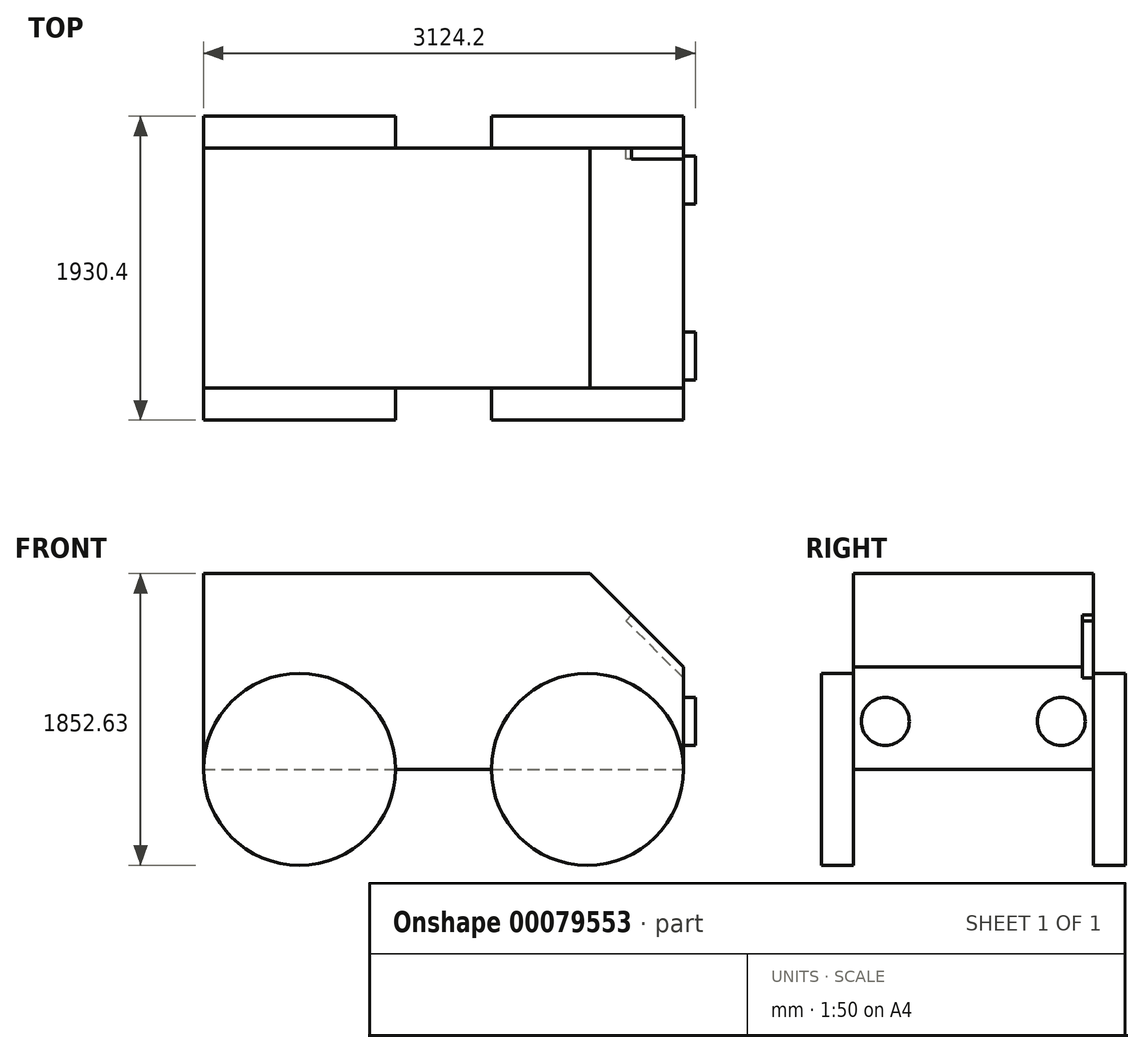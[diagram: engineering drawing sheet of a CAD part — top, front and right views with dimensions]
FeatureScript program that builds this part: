
annotation { "Feature Type Name" : "Feature", "Feature Type Description" : "" }
export const myFeature = defineFeature(function(context is Context, id is Id, definition is map)
    precondition{}
    {
        {
            var Q0;
            Q0=qCreatedBy(makeId("Front.planeOp"),FACE);
            var sketch = newSketch(context, id + "F0", { "sketchPlane" : qUnion([Q0])});
            skLineSegment(sketch, "E0", {"start": v(0, 0) * mm, "end": v(1522.8, 0) * mm});
            skLineSegment(sketch, "E1", {"start": v(1522.8, 0) * mm, "end": v(1522.8, 651.7) * mm});
            skLineSegment(sketch, "E2", {"start": v(1522.8, 651.7) * mm, "end": v(931.48, 1243.03) * mm});
            skLineSegment(sketch, "E3", {"start": v(931.48, 1243.03) * mm, "end": v(-1525.2, 1243.03) * mm});
            skLineSegment(sketch, "E4", {"start": v(-1525.2, 1243.03) * mm, "end": v(-1525.2, 0) * mm});
            skLineSegment(sketch, "E5", {"start": v(-1525.2, 0) * mm, "end": v(0, 0) * mm});
            skSolve(sketch);
        }
        {
            var Q0;
            Q0=makeQuery(id+"F0.imprint","IMPRINT",FACE,{"disambiguationData":[TD([[makeQuery(id+"F0.imprint","IMPRINT",EDGE,{"derivedFrom":sQuery(id+"F0.wireOp",EDGE,"E0")}),1.0]])]});
            extrude(context, id + "F1", {"entities" : qUnion([Q0]), "depth" : 1524 * mm});
        }
        {
            var Q0;
            Q0=makeQuery(id+"F1.opExtrude","SWEPT_FACE",FACE,{"disambiguationData":[OSD([sQuery(id+"F0.wireOp",EDGE,"E1")])]});
            var sketch = newSketch(context, id + "F2", { "sketchPlane" : qUnion([Q0])});
            skCircle(sketch, "E6", {"center": v(-203.2, 304.8) * mm, "radius": 152.4 * mm});
            skCircle(sketch, "E7", {"center": v(-1320.8, 304.8) * mm, "radius": 152.4 * mm});
            skSolve(sketch);
        }
        {
            var Q0;
            Q0 = qSketchRegion(id + "F2", true);
            extrude(context, id + "F3", {"entities" : qUnion([Q0]), "operationType" : NewBodyOperationType.ADD, "depth" : 76.2 * mm});
        }
        {
            var Q0;
            Q0=makeQuery(id+"F1.opExtrude","SWEPT_FACE",FACE,{"disambiguationData":[OSD([sQuery(id+"F0.wireOp",EDGE,"E2")])]});
            var sketch = newSketch(context, id + "F4", { "sketchPlane" : qUnion([Q0])});
            skLineSegment(sketch, "E8.bottom", {"start": v(-67.9, -1371.6) * mm, "end": v(463.56, -1371.6) * mm});
            skLineSegment(sketch, "E8.top", {"start": v(-67.9, -152.4) * mm, "end": v(463.56, -152.4) * mm});
            skLineSegment(sketch, "E8.left", {"start": v(-67.9, -1371.6) * mm, "end": v(-67.9, -152.4) * mm});
            skLineSegment(sketch, "E8.right", {"start": v(463.56, -1371.6) * mm, "end": v(463.56, -152.4) * mm});
            skSolve(sketch);
        }
        {
            var Q0;
            Q0 = qSketchRegion(id + "F4", true);
            extrude(context, id + "F5", {"entities" : qUnion([Q0]), "operationType" : NewBodyOperationType.REMOVE, "oppositeDirection" : true, "depth" : 50.8 * mm});
        }
        {
            var Q0;
            Q0=makeQuery(id+"F1.opExtrude","CAP_FACE",FACE,{"disambiguationData":[OSD([sQuery(id+"F0.wireOp",EDGE,"E0"),sQuery(id+"F0.wireOp",EDGE,"E1"),sQuery(id+"F0.wireOp",EDGE,"E2"),sQuery(id+"F0.wireOp",EDGE,"E3"),sQuery(id+"F0.wireOp",EDGE,"E4"),sQuery(id+"F0.wireOp",EDGE,"E5")])],"isStart":true});
            var sketch = newSketch(context, id + "F6", { "sketchPlane" : qUnion([Q0])});
            skCircle(sketch, "E9", {"center": v(-913.2, 0) * mm, "radius": 609.6 * mm});
            skCircle(sketch, "E10", {"center": v(915.6, 0) * mm, "radius": 609.6 * mm});
            skSolve(sketch);
        }
        {
            var Q0;
            Q0 = qSketchRegion(id + "F6", true);
            extrude(context, id + "F7", {"entities" : qUnion([Q0]), "operationType" : NewBodyOperationType.ADD, "depth" : 203.2 * mm});
        }
        {
            var Q0;
            Q0=makeQuery(id+"F1.opExtrude","CAP_FACE",FACE,{"disambiguationData":[OSD([sQuery(id+"F0.wireOp",EDGE,"E0"),sQuery(id+"F0.wireOp",EDGE,"E1"),sQuery(id+"F0.wireOp",EDGE,"E2"),sQuery(id+"F0.wireOp",EDGE,"E3"),sQuery(id+"F0.wireOp",EDGE,"E4"),sQuery(id+"F0.wireOp",EDGE,"E5")])],"isStart":false});
            var sketch = newSketch(context, id + "F8", { "sketchPlane" : qUnion([Q0])});
            skCircle(sketch, "E11", {"center": v(-915.6, 0) * mm, "radius": 609.6 * mm});
            skCircle(sketch, "E12", {"center": v(913.2, 0) * mm, "radius": 609.6 * mm});
            skSolve(sketch);
        }
        {
            var Q0;
            Q0 = qSketchRegion(id + "F8", true);
            extrude(context, id + "F9", {"entities" : qUnion([Q0]), "operationType" : NewBodyOperationType.ADD, "depth" : 203.2 * mm});
        }
    });
